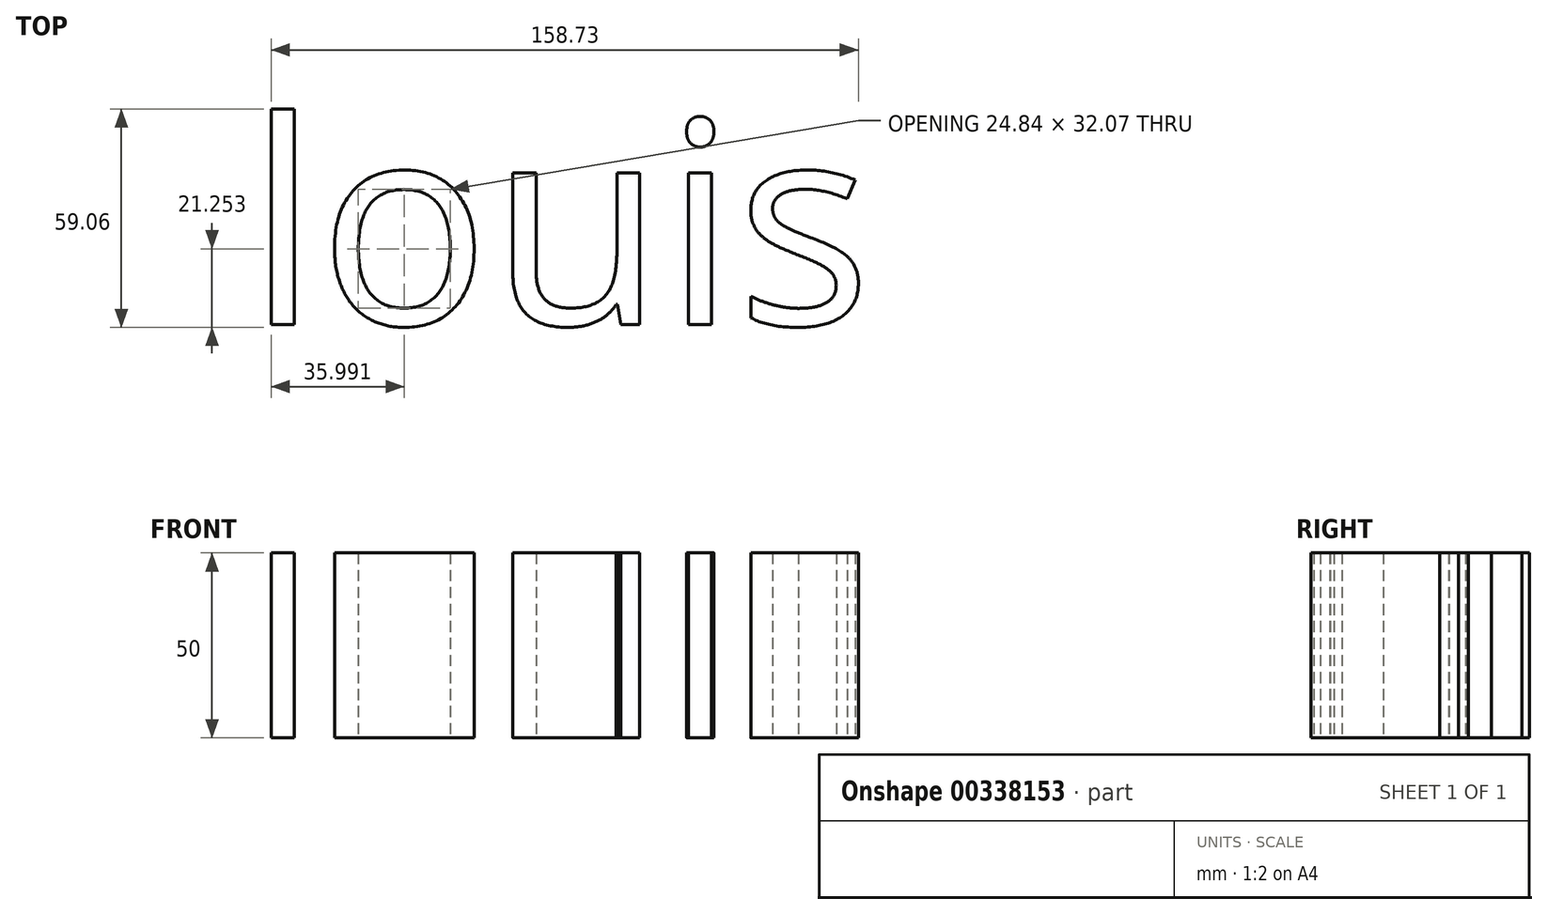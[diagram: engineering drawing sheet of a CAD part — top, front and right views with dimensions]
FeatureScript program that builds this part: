
annotation { "Feature Type Name" : "Feature", "Feature Type Description" : "" }
export const myFeature = defineFeature(function(context is Context, id is Id, definition is map)
    precondition{}
    {
        {
            var Q0;
            Q0=qCreatedBy(makeId("Top.planeOp"),FACE);
            var sketch = newSketch(context, id + "F0", { "sketchPlane" : qUnion([Q0])});
            skText(sketch, "E0", { "text": "louis", "fontName": "OpenSans-Regular.ttf"});
            const initialGuessF0  = {"E0": [-0.1703, -0.05524, 1, 0, 0.05524]};
            skSetInitialGuess(sketch, initialGuessF0);
            skSolve(sketch);
        }
        {
            var Q0;
            Q0 = qSketchRegion(id + "F0", true);
            extrude(context, id + "F1", {"entities" : qUnion([Q0]), "depth" : 50 * mm});
        }
    });
